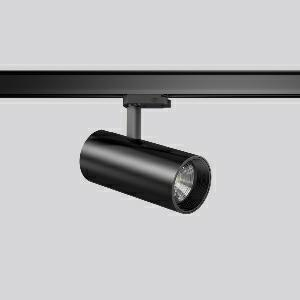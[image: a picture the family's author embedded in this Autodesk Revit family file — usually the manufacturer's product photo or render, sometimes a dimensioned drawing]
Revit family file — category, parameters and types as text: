
# Revit family: deecos_s_mini_742200_003_3_027e
name_source: partatom
category: Lighting Fixtures
units: mm (PartAtom-declared; Revit-internal decimal feet)

## family parameters
Cut with Voids When Loaded = No
Host = Face
Light Source = No
Part Type = Normal
Room Calculation Point = No
Round Connector Dimension = Use Diameter
Shared = No

## types (1)
- DEECOS S mini (1 x LED Modul 935, 2000 lm, 3500)
    Apparent Load = 20 VA
    Approval mark = CE
    CIE Flux Codes = 98 100 100 100 100
    Color Rendering = 92
    Color Temperature = 3500
    Default Elevation = 1800 mm
    Description = Series: DEECOS S mini
LED surface-mounted projector in modern design with no visible cooling ribs. Housing: die-cast aluminium, powder-coated. Rotation range: 356°. Swivel range: 90°. Black plastic ring and recessed LED to prevent glare from the side. Optical assembly with lens made of plastic (polycarbonate) for the best homogeneous light distribution - can be changed without tools. Best colour rendering index Ra>90. With multi adaptor for 3-circuit tracks 230 V. Suitable for Track on ceiling, Wall track. High quality converter without flickering and stroboscopic effect. The following accessories can be mounted without use of tools: interchangeable lenses, decorative glasses, honeycomb louvre, clear and frosted diffusers, white interchangeable plastic ring. 
Colour: deep black, matt (RAL 9005)
Diameter: 87 mm
Height: 214 mm
Lamp: LED
Socket: without socket
Colour temperature: 3500K
Colour rendering index (CRI): 92
System power: 20 W
Rated luminous flux: 2000 lm
Luminous efficiency: 100 lm/W
Control gear: Regulated power supply
Protection class: I
Type of protection: IP 20
    Height = 214 mm
    Lamp = 1 x LED Modul 935
    Lamp Light Flux = 2000 lm
    Lamp count = 1
    Length = 87 mm
    Lifetime = 50000 h
    Luminous efficacy = 100 lm/W
    Manufacturer = RZB
    ModVariant = No
    Model = 742200.003.3
    Mounting Place = Ceiling
    Mounting Type = Rail mounted
    Number of Poles = 1
    OnlyDefault = Yes
    Power Factor = 1
    Product Name = DEECOS S mini
    Product group = Track mounted projectors
    ProductGroupID = 301
    Protection Class = Protection class I
    Protection Degree = IP 20
    RLX_Detail_Level = 1
    RLX_Emergency_Light_Flux = 0 lm
    RLX_Emergency_Type = 0
    RLX_Emergency_Type_DB = No
    RlxData = <blob elided: 38569 chars, md5=1f9377a6>
    Socket = socket
    Standby Power = 0 W
    System Light Flux = 2000 lm
    System Power = 20 W
    Type Comments = Product without accessories
    Type Image = 741930.003.jpg
    URL = http://relux.com
    VarID = ---
    Voltage = 230 V
    Voltage Range = 220-240 V
    Weight = 0.00 kg
    Width = 0 mm  [stored 0 ft]

note: [stored X ft] marks values corroborated as IEEE doubles in the binary element streams (Revit-internal decimal feet)

## geometry (parser evidence)
native form markers: Blend x4, Sweep x12
no freeform markers — native parametric forms only
